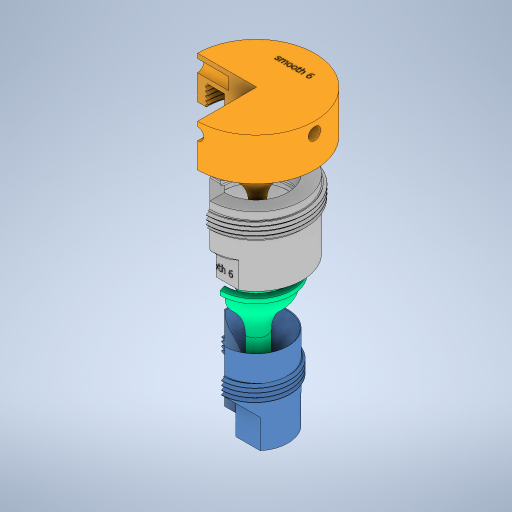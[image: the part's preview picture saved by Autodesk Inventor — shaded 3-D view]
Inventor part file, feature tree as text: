
AUTODESK INVENTOR PART (.ipt)
format: ipt  version: 2023.3 (Build 273359000, 359)  size: 4,286,464 bytes
history: native  units: mm
features: sketch x20, other x10, thicken_offset x10, move_body x6, extrude x5, revolve x4, surface_op x4, chamfer x4, boolean_combine x3, plane x3, hole x3, emboss x3, split x2, helix x2, loft x1, pattern_circular x1, direct_edit x1, projected_geometry x1
ambient origin geometry x8: Origin, YZ Plane, XZ Plane, XY Plane, X Axis, Y Axis, Z Axis, Center Point
bodies: Solid2 (feature_tree), Solid1 (feature_tree), Solid3 (feature_tree), Solid4 (feature_tree), Solid6 (feature_tree), Solid1_1 (feature_tree)
feature tree (83):
  other  "rod_seal_friction.ipt"
  revolve  "Revolution1"  [1 undecoded]
  boolean_combine  "Combine1"
  surface_op  "Extend1"
  split  "Split1"
  plane  "Work Plane1"
  surface_op  "Stitch Surface1"
  split  "Split2"
  hole  "Hole1"  [1 undecoded]
  loft  "Loft1"
  thicken_offset  "Thicken1"
  sketch  "Sketch11"  dims[d23=5.0mm d24=0.0mm d25=90.0deg]
  helix  "Coil1"  [1 undecoded]
  boolean_combine  "Combine2"
  thicken_offset  "Thicken2"
  extrude  "Extrusion2"  Depth=5.0mm
  chamfer  "Chamfer1"  Angle=90.0deg  [1 undecoded]
  thicken_offset  "Thicken8"
  thicken_offset  "Thicken9"
  extrude  "Extrusion3"  Depth=0.15mm
  extrude  "Extrusion7"  TaperAngle=60.0deg  [1 undecoded]
  revolve  "Revolution13"  [1 undecoded]
  thicken_offset  "Thicken23"
  thicken_offset  "Thicken20"
  chamfer  "Chamfer6"  Distance=16.0mm
  plane  "Work Plane2"
  helix  "Coil5"  [1 undecoded]
  extrude  "Extrusion4"  Depth=3.0mm
  boolean_combine  "Combine5"
  hole  "Hole2"  [1 undecoded]
  thicken_offset  "Thicken19"
  thicken_offset  "Thicken24"
  revolve  "Revolution12"  [1 undecoded]
  extrude  "Extrusion10"  Depth=10.0mm
  chamfer  "Chamfer3"  Distance=0.2mm
  emboss  "Emboss3"
  thicken_offset  "Thicken21"
  plane  "Work Plane3"
  hole  "Hole3"  [1 undecoded]
  pattern_circular  "Circular Pattern2"  [2 undecoded]
  revolve  "Revolution7"  [1 undecoded]
  chamfer  "Chamfer4"  Distance=55.0mm
  thicken_offset  "Thicken22"
  emboss  "Emboss4"
  emboss  "Emboss5"
  direct_edit  "Direct Edit1"
  other  "Solid1::rod_seal_friction.ipt"
  other  "TaggingFeature1"
  other  "Srf1"
  sketch  "Sketch1"  dims[d0=10.0mm d3=7.5mm d5=5.0mm d6=17.453293mm]
  sketch  "Sketch2"  dims[d2=13.0mm d4=10.0mm]
  projected_geometry  "Projected Loop1"
  other  "Srf2"
  sketch  "Sketch3"  dims[d7=360.0deg d8=16.75mm d9=-2.5mm]
  other  "Srf3"
  other  "Srf4"
  sketch  "Sketch4"  dims[d11=0.0mm d12=5.0mm]
  sketch  "Sketch5"  dims[d13=5.0mm]
  sketch  "Sketch6"  dims[d14=0.0mm]
  sketch  "Sketch7"  dims[d15=1.0mm d16=6.0mm d17=4.0mm d18=2.0mm d19=90.0deg d20=6.0mm d21=20.594885mm]
  sketch  "Sketch10"  dims[d22=1.0mm]
  sketch  "Sketch13"  dims[d26=0.0mm d27=90.0deg]
  sketch  "Sketch14"  dims[d28=1.0mm d29=6.0mm d30=4.0mm d31=2.0mm d32=90.0deg d33=7.0mm d34=20.594885mm d35=0.15mm d36=0.15mm]
  sketch  "Sketch18"  dims[d41=0.3mm d42=0.0mm]
  sketch  "Sketch26"  dims[d49=2.0mm d50=10.0mm d51=50.0mm d52=0.0mm d53=90.0deg d54=90.0deg d55=0.0mm d56=0.0mm d57=60.0deg]
  sketch  "Sketch28"  dims[d58=60.0deg d61=22.0mm d62=16.0mm d73=16.0mm d74=0.0mm d75=2.0mm d76=2.0mm d77=45.0deg]
  sketch  "Sketch29"  dims[d78=3.0mm d79=3.0mm]
  sketch  "Sketch33"  dims[d80=6.0mm d81=6.0mm]
  sketch  "Sketch36"  dims[d83=10.0mm d84=0.0mm d94=9.599311mm]
  sketch  "Sketch37"  dims[d106=10.0mm d107=0.0mm d142=9.599311mm]
  sketch  "Sketch38"  dims[d154=7.0mm]
  sketch  "Sketch39"  dims[d156=0.1mm d157=0.2mm d158=0.1mm d159=4.0mm d160=27.0mm d161=0.0mm d168=45.0mm d169=55.0mm d170=39.0mm d171=10.0mm d174=10.0mm d175=0.0mm d179=2.6mm d180=2.0mm d181=45.0deg d184=5.0mm d185=5.0mm d186=5.95mm d187=6.0mm d188=4.0mm d189=2.0mm d190=90.0deg d191=15.0mm d192=0.0mm d193=40.0mm d194=360.0deg d196=0.15mm d197=2.0mm d198=90.0deg d199=3.6mm d200=2.0mm d201=45.0deg d212=9.599311mm d227=9.599311mm d228=0.320166mm d229=0.320166mm d232=2.0mm d234=9.599311mm d238=2.002mm d239=14.0mm d240=10.0mm d241=0.0mm d242=0.0mm d243=0.0mm d244=0.0mm d245=0.0mm d246=0.17mm d247=90.0deg d248=2.0mm d249=2.0mm d250=45.0deg d251=0.1mm d252=0.1mm d253=0.05mm d254=90.0deg d255=0.35mm d256=0.15mm d257=0.1mm d258=0.1mm d259=0.3mm d260=0.0mm d261=0.3mm d262=0.0mm d263=10.0mm d264=0.0mm d265=0.0mm d266=37.5mm d267=0.0mm d268=0.0mm d269=-44.0mm d270=0.0mm d271=14.5mm d272=0.0mm d273=0.0mm d274=-17.25mm d275=0.0mm d276=0.0mm d277=-3.0mm d278=0.0mm d279=0.0mm d280=0.0mm d281=5.5mm d176=0.5mm d177=0.872665mm]
  other  "Solid1::rod_seal_friction.ipt_1"
  other  "TaggingFeature2"
  other  "Srf10::Derived"
  surface_op  "Boundary Patch1"
  surface_op  "Boundary Patch2"
  move_body  "Move1"
  move_body  "Move2"
  move_body  "Move3"
  move_body  "Move4"
  move_body  "Move5"
  move_body  "Move6"
note: 13 required parameter values undecoded (feature->parameter linkage not recoverable at this tier; creation-order binding heuristic only, values carry confidence <= 0.55)